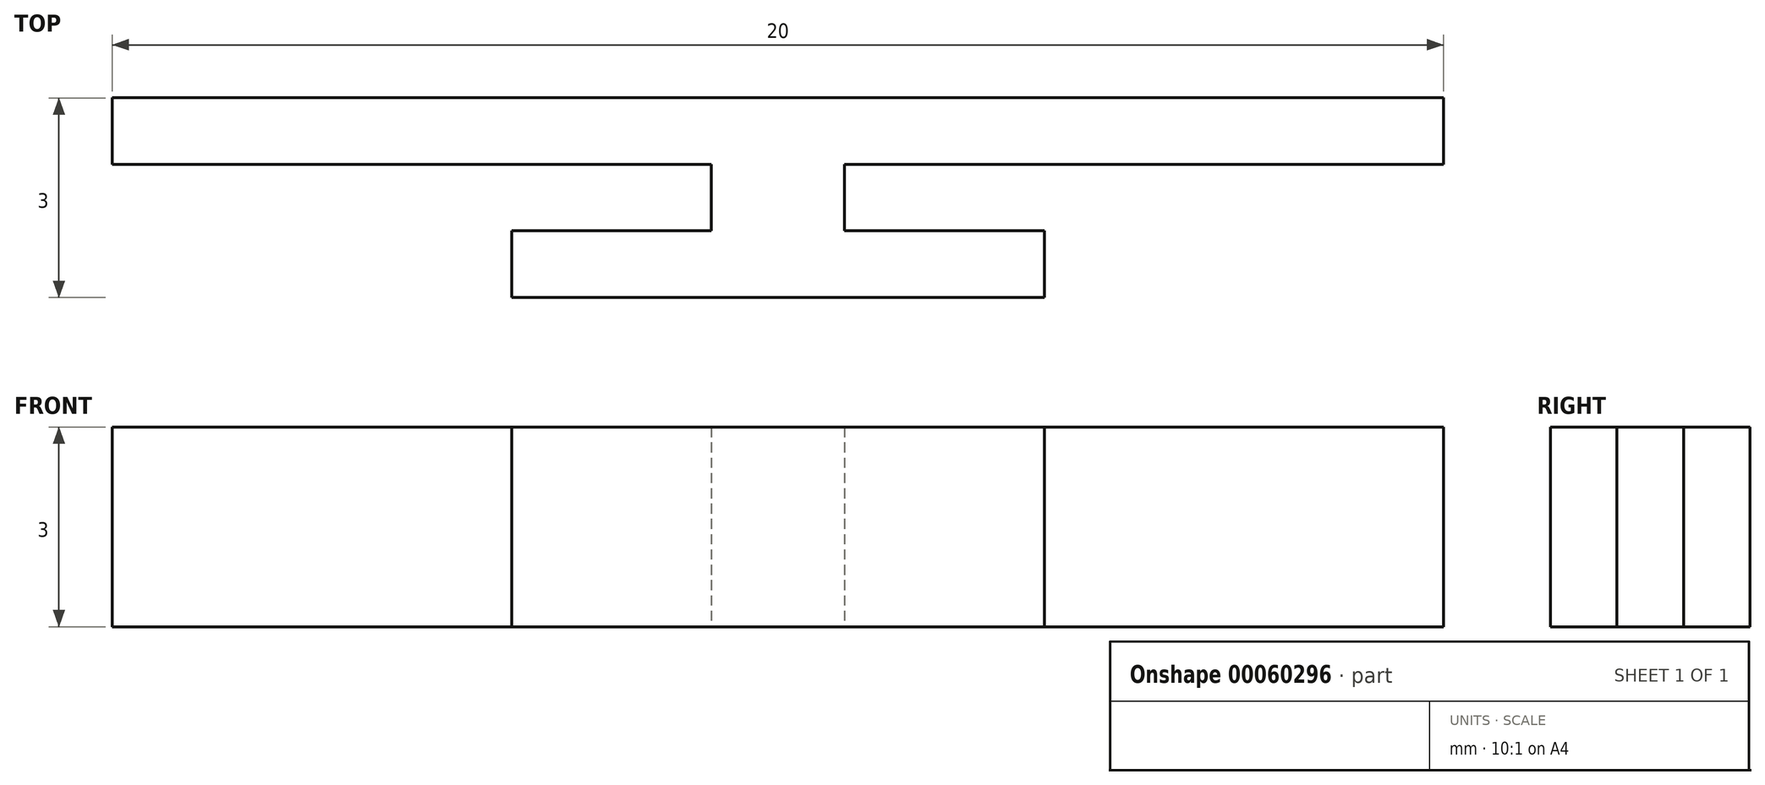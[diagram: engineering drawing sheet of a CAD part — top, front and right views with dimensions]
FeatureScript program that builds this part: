
annotation { "Feature Type Name" : "Feature", "Feature Type Description" : "" }
export const myFeature = defineFeature(function(context is Context, id is Id, definition is map)
    precondition{}
    {
        {
            var Q0;
            Q0=qCreatedBy(makeId("Top.planeOp"),FACE);
            var sketch = newSketch(context, id + "F0", { "sketchPlane" : qUnion([Q0])});
            skLineSegment(sketch, "E0.bottom", {"start": v(-10, 9.46) * mm, "end": v(10, 9.46) * mm});
            skLineSegment(sketch, "E0.top", {"start": v(-10, 8.46) * mm, "end": v(10, 8.46) * mm});
            skLineSegment(sketch, "E0.left", {"start": v(-10, 9.46) * mm, "end": v(-10, 8.46) * mm});
            skLineSegment(sketch, "E0.right", {"start": v(10, 9.46) * mm, "end": v(10, 8.46) * mm});
            skLineSegment(sketch, "E1.bottom", {"start": v(0, 8.46) * mm, "end": v(0, 8.46) * mm});
            skLineSegment(sketch, "E1.top", {"start": v(0, 7.46) * mm, "end": v(0, 7.46) * mm});
            skLineSegment(sketch, "E1.left", {"start": v(0, 8.46) * mm, "end": v(0, 7.46) * mm});
            skLineSegment(sketch, "E1.right", {"start": v(0, 8.46) * mm, "end": v(0, 7.46) * mm});
            skLineSegment(sketch, "E2.bottom", {"start": v(-4, 7.46) * mm, "end": v(4, 7.46) * mm});
            skLineSegment(sketch, "E2.top", {"start": v(-4, 6.46) * mm, "end": v(4, 6.46) * mm});
            skLineSegment(sketch, "E2.left", {"start": v(-4, 7.46) * mm, "end": v(-4, 6.46) * mm});
            skLineSegment(sketch, "E2.right", {"start": v(4, 7.46) * mm, "end": v(4, 6.46) * mm});
            skLineSegment(sketch, "E3", {"start": v(0, 9.46) * mm, "end": v(0, 8.46) * mm});
            skLineSegment(sketch, "E4", {"start": v(0, 7.46) * mm, "end": v(0, 6.46) * mm});
            skLineSegment(sketch, "E5", {"start": v(1, 8.46) * mm, "end": v(1, 7.46) * mm});
            skLineSegment(sketch, "E6", {"start": v(-1, 8.46) * mm, "end": v(-1, 7.46) * mm});
            skSolve(sketch);
        }
        {
            var Q0;
            Q0 = qSketchRegion(id + "F0", true);
            extrude(context, id + "F1", {"entities" : qUnion([Q0]), "depth" : 3 * mm});
        }
    });
